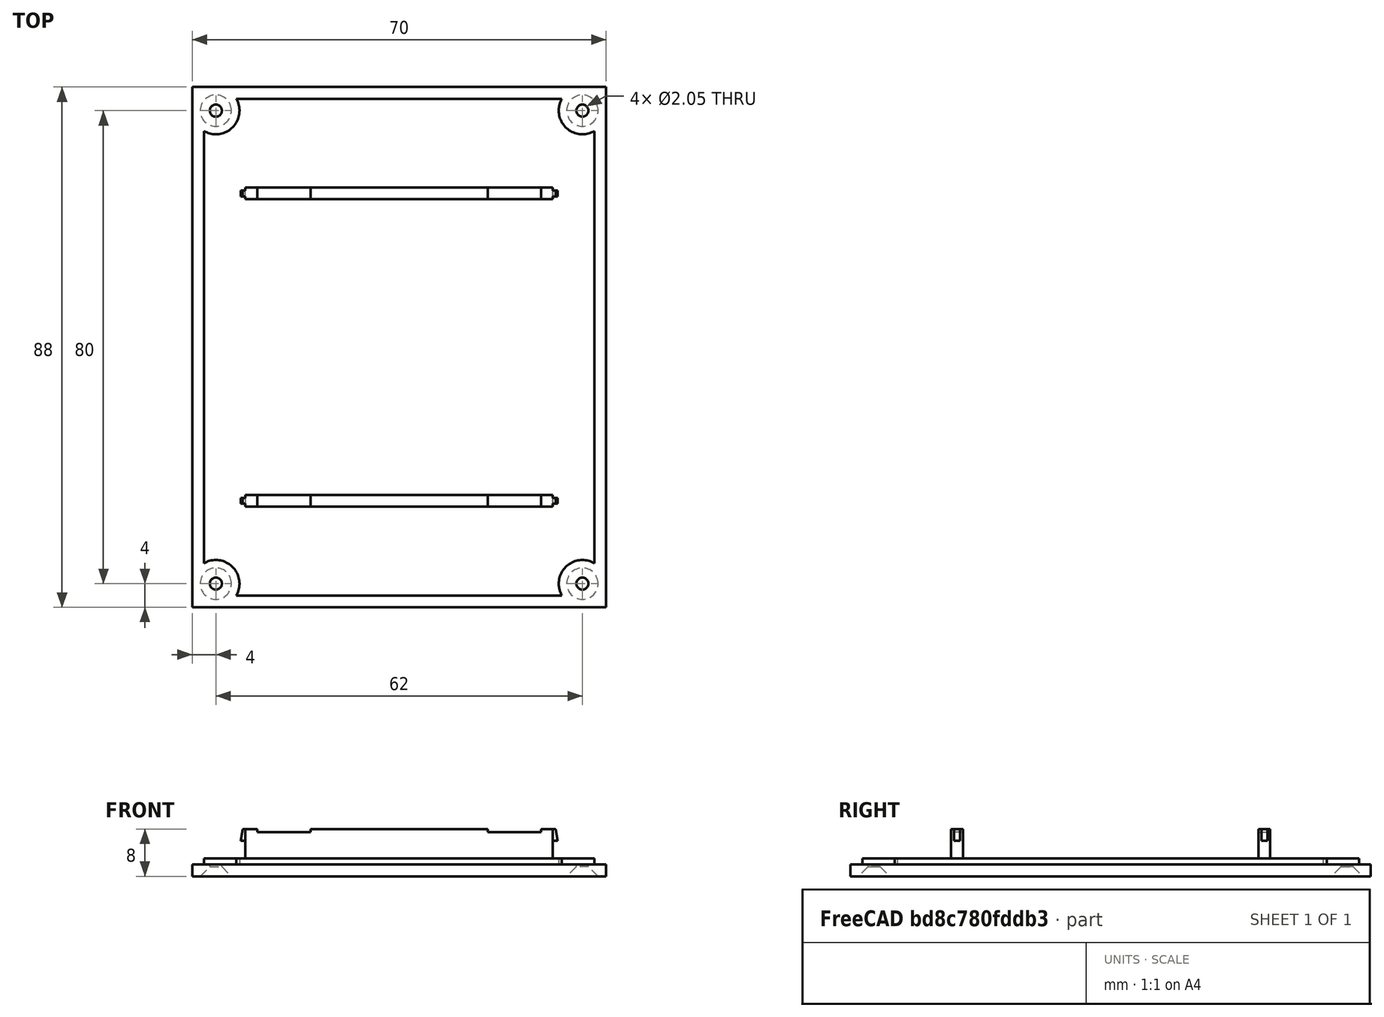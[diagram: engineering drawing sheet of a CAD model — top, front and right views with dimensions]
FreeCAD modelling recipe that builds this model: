
FCSTD DOCUMENT  (FreeCAD 0.19R)
Label: rebus-chipset-bottom
License: All rights reserved
LicenseURL: http://en.wikipedia.org/wiki/All_rights_reserved
objects: PartDesign::Mirrored×11, Sketcher::SketchObject×9, PartDesign::MultiTransform×6, PartDesign::Pad×4, PartDesign::Pocket×3, PartDesign::Hole×1, PartDesign::Body×1, Mesh::Feature×1
note: 43 computed .brp shape members not serialized (recipe doc carries the construction recipe); baked Part::Feature solids carry a one-line shape summary decoded from their .brp

FEATURE [Sketcher::SketchObject] Sketch
  FullyConstrained = true
  MapMode = 5
  Support = -> [XY_Plane]
  sketch-geometry (4):
    g0: LineSegment StartX=-35 StartY=44 StartZ=0 EndX=35 EndY=44 EndZ=0
    g1: LineSegment StartX=35 StartY=44 StartZ=0 EndX=35 EndY=-44 EndZ=0
    g2: LineSegment StartX=35 StartY=-44 StartZ=0 EndX=-35 EndY=-44 EndZ=0
    g3: LineSegment StartX=-35 StartY=-44 StartZ=0 EndX=-35 EndY=44 EndZ=0
  constraints (12):
    c: Coincident(g0,g1)
    c: Coincident(g1,g2)
    c: Coincident(g2,g3)
    c: Coincident(g3,g0)
    c: Horizontal(g0)
    c: Horizontal(g2)
    c: Vertical(g1)
    c: Vertical(g3)
    c: DistanceX(g0,g0) = 70
    c: DistanceY(g1,g1) = 88
    c: DistanceX(g-1,g0) = 35
    c: DistanceY(g-1,g0) = 44
FEATURE [PartDesign::Pad] Pad  label="Base support"
  Direction = (1,1,1)
  Length = 2
  Length2 = 100
  Profile = -> Sketch
  Type = 0
FEATURE [Sketcher::SketchObject] Sketch001
  ExternalGeometry = -> [Pad]
  FullyConstrained = true
  MapMode = 5
  Placement = pos=(0,0,2) rot=(0,0,1;0rad)
  Support = -> [Pad]
  sketch-geometry (4):
    g0: LineSegment StartX=-33 StartY=42 StartZ=0 EndX=33 EndY=42 EndZ=0
    g1: LineSegment StartX=33 StartY=42 StartZ=0 EndX=33 EndY=-42 EndZ=0
    g2: LineSegment StartX=33 StartY=-42 StartZ=0 EndX=-33 EndY=-42 EndZ=0
    g3: LineSegment StartX=-33 StartY=-42 StartZ=0 EndX=-33 EndY=42 EndZ=0
  constraints (12):
    c: Coincident(g0,g1)
    c: Coincident(g1,g2)
    c: Coincident(g2,g3)
    c: Coincident(g3,g0)
    c: Horizontal(g0)
    c: Horizontal(g2)
    c: Vertical(g1)
    c: Vertical(g3)
    c: DistanceY(g0,g-3) = 2
    c: DistanceX(g-3,g0) = 2
    c: DistanceX(g1,g-4) = 2
    c: DistanceY(g-4,g1) = 2
FEATURE [PartDesign::Pad] Pad001  label="Base"
  BaseFeature = -> Pad
  Direction = (1,1,1)
  Length = 1
  Length2 = 100
  Profile = -> Sketch001
  Type = 0
FEATURE [Sketcher::SketchObject] Sketch003
  FullyConstrained = false
  MapMode = 5
  Placement = pos=(0,0,0) rot=(1,0,0;3.14159rad)
  sketch-geometry (1):
    g0: Circle CenterX=-31 CenterY=40 CenterZ=0 NormalX=0 NormalY=0 NormalZ=1 AngleXU=0 Radius=1.25
  constraints (1):
    c: Radius(g0) = 1.25
FEATURE [PartDesign::Hole] Hole  label="Screw hole"
  BaseFeature = -> Pad001
  Depth = 3
  DepthType = 0
  Diameter = 2.05
  DrillForDepth = false
  DrillPoint = 1
  DrillPointAngle = 118
  HoleCutCountersinkAngle = 90
  HoleCutCustomValues = false
  HoleCutDepth = 2.5625
  HoleCutDiameter = 5.3
  HoleCutType = 6
  ModelActualThread = false
  Profile = -> Sketch003
  Tapered = false
  TaperedAngle = 90
  ThreadAngle = 60
  ThreadClass = 0
  ThreadCutOffInner = 0.0487139
  ThreadCutOffOuter = 0.0974279
  ThreadDirection = 0
  ThreadFit = 0
  ThreadPitch = 0.45
  ThreadSize = 8
  ThreadType = 1
  Threaded = true
FEATURE [PartDesign::Mirrored] Mirrored001
  MirrorPlane = -> XZ_Plane
FEATURE [PartDesign::Mirrored] Mirrored002
  MirrorPlane = -> YZ_Plane
FEATURE [PartDesign::MultiTransform] MultiTransform  label="Screw hole replication"
  BaseFeature = -> Hole
  Originals = -> [Hole]
  Transformations = -> [Mirrored001,Mirrored002]
FEATURE [Sketcher::SketchObject] Sketch004
  FullyConstrained = true
  MapMode = 5
  Placement = pos=(0,0,3) rot=(0,0,1;0rad)
  Support = -> [MultiTransform]
  sketch-geometry (4):
    g0: LineSegment StartX=-26 StartY=27 StartZ=0 EndX=26 EndY=27 EndZ=0
    g1: LineSegment StartX=26 StartY=27 StartZ=0 EndX=26 EndY=25 EndZ=0
    g2: LineSegment StartX=26 StartY=25 StartZ=0 EndX=-26 EndY=25 EndZ=0
    g3: LineSegment StartX=-26 StartY=25 StartZ=0 EndX=-26 EndY=27 EndZ=0
  constraints (12):
    c: Coincident(g0,g1)
    c: Coincident(g1,g2)
    c: Coincident(g2,g3)
    c: Coincident(g3,g0)
    c: Horizontal(g0)
    c: Horizontal(g2)
    c: Vertical(g1)
    c: Vertical(g3)
    c: DistanceX(g0,g0) = 52
    c: DistanceY(g1,g1) = 2
    c: DistanceX(g-1,g1) = 26
    c: DistanceY(g-1,g1) = 25
FEATURE [PartDesign::Pad] Pad002  label="Chipset support"
  BaseFeature = -> MultiTransform
  Direction = (1,1,1)
  Length = 5
  Length2 = 100
  Profile = -> Sketch004
  Type = 0
FEATURE [Sketcher::SketchObject] Sketch005
  ExternalGeometry = -> [Pad002]
  FullyConstrained = true
  MapMode = 5
  Placement = pos=(0,0,8) rot=(0,0,1;0rad)
  Support = -> [Pad002]
  sketch-geometry (4):
    g0: LineSegment StartX=-24 StartY=27 StartZ=0 EndX=-15 EndY=27 EndZ=0
    g1: LineSegment StartX=-15 StartY=27 StartZ=0 EndX=-15 EndY=25 EndZ=0
    g2: LineSegment StartX=-15 StartY=25 StartZ=0 EndX=-24 EndY=25 EndZ=0
    g3: LineSegment StartX=-24 StartY=25 StartZ=0 EndX=-24 EndY=27 EndZ=0
  constraints (12):
    c: Coincident(g0,g1)
    c: Coincident(g1,g2)
    c: Coincident(g2,g3)
    c: Coincident(g3,g0)
    c: Horizontal(g0)
    c: Horizontal(g2)
    c: Vertical(g1)
    c: Vertical(g3)
    c: DistanceX(g-3,g0) = 2
    c: DistanceX(g0,g0) = 9
    c: Equal(g3,g-5)
    c: Horizontal(g0,g-5)
FEATURE [PartDesign::Pocket] Pocket  label="Chipset support pocket"
  BaseFeature = -> Pad002
  Length = 0.5
  Length2 = 100
  Profile = -> Sketch005
  Type = 0
FEATURE [PartDesign::Mirrored] Mirrored
  MirrorPlane = -> XZ_Plane
FEATURE [PartDesign::MultiTransform] MultiTransform001  label="Chipset support replication"
  BaseFeature = -> Pocket
  Originals = -> [Pad002]
  Transformations = -> [Mirrored]
FEATURE [PartDesign::Mirrored] Mirrored003
  MirrorPlane = -> XZ_Plane
FEATURE [PartDesign::Mirrored] Mirrored004
  MirrorPlane = -> YZ_Plane
FEATURE [PartDesign::MultiTransform] MultiTransform002  label="Chipset support pocket replication"
  BaseFeature = -> MultiTransform001
  Originals = -> [Pocket]
  Transformations = -> [Mirrored003,Mirrored004]
FEATURE [Sketcher::SketchObject] Sketch006
  ExternalGeometry = -> [MultiTransform002]
  FullyConstrained = true
  MapMode = 5
  Placement = pos=(0,27,0) rot=(0,0.707107,0.707107;3.14159rad)
  Support = -> [MultiTransform002]
  sketch-geometry (4):
    g0: LineSegment StartX=26 StartY=8 StartZ=0 EndX=26.5 EndY=8 EndZ=0
    g1: LineSegment StartX=26.5 StartY=8 StartZ=0 EndX=26.8 EndY=6 EndZ=0
    g2: LineSegment StartX=26.8 StartY=6 StartZ=0 EndX=26 EndY=6 EndZ=0
    g3: LineSegment StartX=26 StartY=6 StartZ=0 EndX=26 EndY=8 EndZ=0
  constraints (11):
    c: Horizontal(g0)
    c: Coincident(g0,g1)
    c: Coincident(g1,g2)
    c: Coincident(g2,g3)
    c: Coincident(g3,g0)
    c: Vertical(g3)
    c: DistanceY(g3,g3) = 2
    c: Horizontal(g2)
    c: DistanceX(g2,g2) = 0.8
    c: DistanceX(g0,g0) = 0.5
    c: Coincident(g0,g-3)
FEATURE [Sketcher::SketchObject] Sketch007
  ExternalGeometry = -> [MultiTransform002]
  FullyConstrained = true
  MapMode = 5
  Placement = pos=(0,0,3) rot=(0,0,1;0rad)
  sketch-geometry (1):
    g0: Circle CenterX=-31 CenterY=40 CenterZ=0 NormalX=0 NormalY=0 NormalZ=1 AngleXU=0 Radius=4
  constraints (3):
    c: Radius(g0) = 4
    c: DistanceX(g-3,g0) = 2
    c: DistanceY(g0,g-3) = 2
FEATURE [PartDesign::Pocket] Pocket001
  BaseFeature = -> MultiTransform002
  Length = 1
  Length2 = 100
  Profile = -> Sketch007
  Type = 0
FEATURE [PartDesign::Mirrored] Mirrored005
  MirrorPlane = -> XZ_Plane
FEATURE [PartDesign::Mirrored] Mirrored006
  MirrorPlane = -> YZ_Plane
FEATURE [PartDesign::MultiTransform] MultiTransform003
  BaseFeature = -> Pocket001
  Originals = -> [Pocket001]
  Transformations = -> [Mirrored005,Mirrored006]
FEATURE [Sketcher::SketchObject] Sketch008
  ExternalGeometry = -> [MultiTransform003]
  FullyConstrained = true
  MapMode = 5
  Placement = pos=(-26,0,0) rot=(0.57735,-0.57735,-0.57735;2.0944rad)
  Support = -> [MultiTransform003]
  sketch-geometry (4):
    g0: LineSegment StartX=-26.5 StartY=8 StartZ=0 EndX=-25.5 EndY=8 EndZ=0
    g1: LineSegment StartX=-25.5 StartY=8 StartZ=0 EndX=-25.5 EndY=6 EndZ=0
    g2: LineSegment StartX=-25.5 StartY=6 StartZ=0 EndX=-26.5 EndY=6 EndZ=0
    g3: LineSegment StartX=-26.5 StartY=6 StartZ=0 EndX=-26.5 EndY=8 EndZ=0
  constraints (12):
    c: Coincident(g0,g1)
    c: Coincident(g1,g2)
    c: Coincident(g2,g3)
    c: Coincident(g3,g0)
    c: Horizontal(g0)
    c: Horizontal(g2)
    c: Vertical(g1)
    c: Vertical(g3)
    c: DistanceX(g0,g0) = 1
    c: Horizontal(g0,g-3)
    c: DistanceY(g1,g1) = 2
    c: DistanceX(g-3,g0) = 0.5
FEATURE [PartDesign::Pad] Pad003
  BaseFeature = -> MultiTransform003
  Direction = (1,1,1)
  Length = 0.8
  Length2 = 100
  Profile = -> Sketch008
  Type = 0
FEATURE [Sketcher::SketchObject] Sketch009
  ExternalGeometry = -> [Pad003]
  FullyConstrained = true
  MapMode = 5
  Placement = pos=(0,26.5,0) rot=(0,0.707107,0.707107;3.14159rad)
  Support = -> [Pad003]
  sketch-geometry (3):
    g0: LineSegment StartX=26.8 StartY=8 StartZ=0 EndX=26.5 EndY=8 EndZ=0
    g1: LineSegment StartX=26.5 StartY=8 StartZ=0 EndX=26.8 EndY=6 EndZ=0
    g2: LineSegment StartX=26.8 StartY=6 StartZ=0 EndX=26.8 EndY=8 EndZ=0
  constraints (8):
    c: Horizontal(g0)
    c: Coincident(g0,g1)
    c: Coincident(g1,g2)
    c: Coincident(g2,g0)
    c: Vertical(g2)
    c: DistanceX(g0,g0) = 0.3
    c: DistanceY(g2,g2) = 2
    c: Coincident(g0,g-3)
FEATURE [PartDesign::Pocket] Pocket002
  BaseFeature = -> Pad003
  Length = 1
  Length2 = 100
  Profile = -> Sketch009
  Type = 0
FEATURE [PartDesign::Mirrored] Mirrored007
  MirrorPlane = -> YZ_Plane
FEATURE [PartDesign::Mirrored] Mirrored008
  MirrorPlane = -> XZ_Plane
FEATURE [PartDesign::MultiTransform] MultiTransform004
  BaseFeature = -> Pocket002
  Originals = -> [Pad003]
  Transformations = -> [Mirrored007,Mirrored008]
FEATURE [PartDesign::Mirrored] Mirrored009
  MirrorPlane = -> YZ_Plane
FEATURE [PartDesign::Mirrored] Mirrored010
  MirrorPlane = -> XZ_Plane
FEATURE [PartDesign::MultiTransform] MultiTransform005
  BaseFeature = -> MultiTransform004
  Originals = -> [Pocket002]
  Transformations = -> [Mirrored009,Mirrored010]
FEATURE [PartDesign::Body] Body
  Group = -> [Sketch,Pad,Sketch001,Pad001,Sketch003,Hole,MultiTransform,Sketch007,Mirrored001,Mirrored002,Sketch004,Pad002,Sketch005,Pocket,MultiTransform001,Mirrored,MultiTransform002,Mirrored003,Mirrored004,Sketch006,Pocket001,MultiTransform003,Mirrored005,Mirrored006,Sketch008,Pad003,Sketch009,Pocket002,MultiTransform004,Mirrored007,Mirrored008,MultiTransform005,Mirrored009,Mirrored010]
  Origin = -> Origin
  Tip = -> MultiTransform005
FEATURE [Mesh::Feature] Mesh  label="MultiTransform005 (Meshed)"
